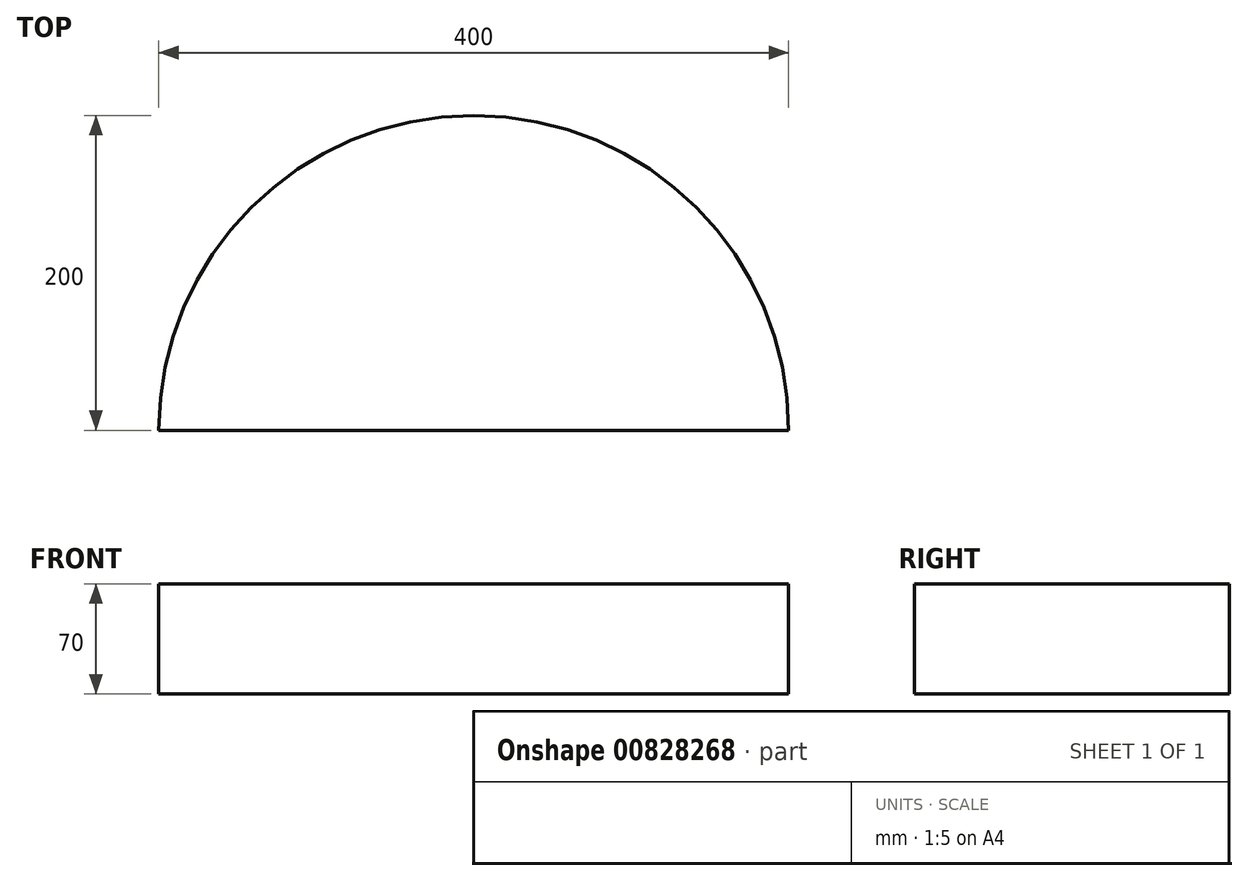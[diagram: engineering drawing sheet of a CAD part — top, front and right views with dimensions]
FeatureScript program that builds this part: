
annotation { "Feature Type Name" : "Feature", "Feature Type Description" : "" }
export const myFeature = defineFeature(function(context is Context, id is Id, definition is map)
    precondition{}
    {
        {
            var Q0;
            Q0=qCreatedBy(makeId("Top.planeOp"),FACE);
            var sketch = newSketch(context, id + "F0", { "sketchPlane" : qUnion([Q0])});
            skArc(sketch, "E0", {"start": v(200, 0) * mm, "mid": v(0, 200) * mm, "end": v(-200, 0) * mm});
            skLineSegment(sketch, "E1", {"start": v(-200, 0) * mm, "end": v(200, 0) * mm});
            skSolve(sketch);
        }
        {
            var Q0;
            Q0=makeQuery(id+"F0.imprint","IMPRINT",FACE,{"disambiguationData":[TD([[makeQuery(id+"F0.imprint","IMPRINT",EDGE,{"derivedFrom":sQuery(id+"F0.wireOp",EDGE,"E0")}),1.0]])]});
            extrude(context, id + "F1", {"entities" : qUnion([Q0]), "depth" : 70 * mm, "offsetDistance" : 25 * mm});
        }
    });
